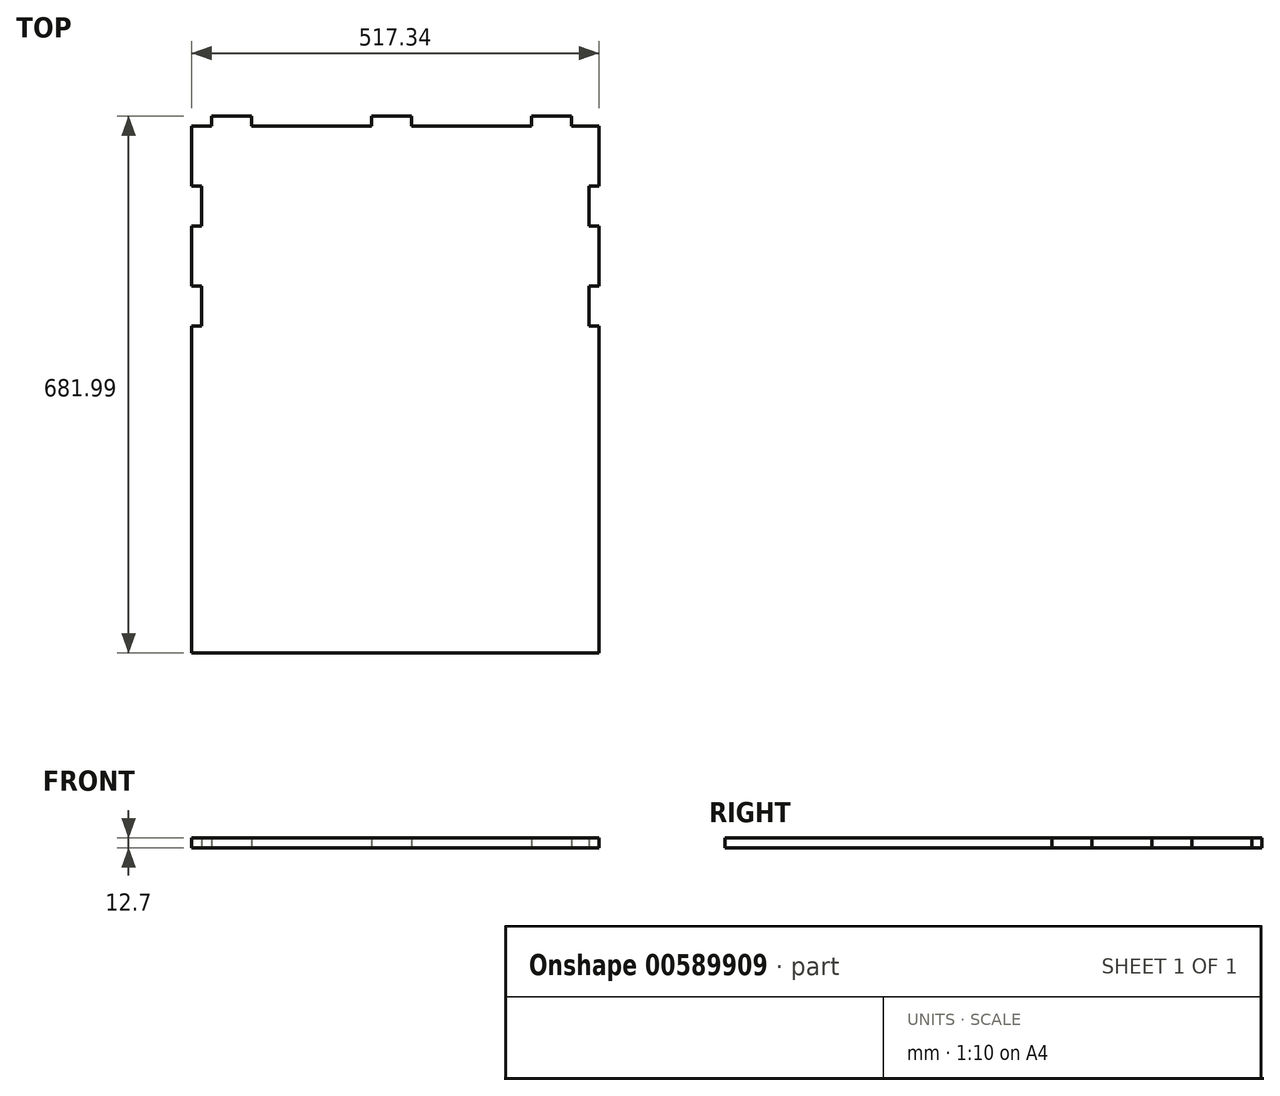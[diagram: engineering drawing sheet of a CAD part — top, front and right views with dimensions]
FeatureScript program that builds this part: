
annotation { "Feature Type Name" : "Feature", "Feature Type Description" : "" }
export const myFeature = defineFeature(function(context is Context, id is Id, definition is map)
    precondition{}
    {
        {
            var Q0;
            Q0=qCreatedBy(makeId("Top.planeOp"),FACE);
            var sketch = newSketch(context, id + "F0", { "sketchPlane" : qUnion([Q0])});
            skLineSegment(sketch, "E0.bottom", {"start": v(-296.76, 491.23) * mm, "end": v(-271.36, 491.23) * mm});
            skLineSegment(sketch, "E0.top", {"start": v(-296.76, -178.06) * mm, "end": v(220.58, -178.06) * mm});
            skLineSegment(sketch, "E0.left", {"start": v(-296.76, 491.23) * mm, "end": v(-296.76, 415.03) * mm});
            skLineSegment(sketch, "E0.right", {"start": v(220.58, 491.23) * mm, "end": v(220.58, 415.03) * mm});
            skLineSegment(sketch, "E1.top", {"start": v(-271.36, 503.93) * mm, "end": v(-220.56, 503.93) * mm});
            skLineSegment(sketch, "E1.left", {"start": v(-271.36, 491.23) * mm, "end": v(-271.36, 503.93) * mm});
            skLineSegment(sketch, "E1.right", {"start": v(-220.56, 491.23) * mm, "end": v(-220.56, 503.93) * mm});
            skLineSegment(sketch, "E2.top", {"start": v(185.84, 503.93) * mm, "end": v(135.04, 503.93) * mm});
            skLineSegment(sketch, "E2.left", {"start": v(185.84, 491.23) * mm, "end": v(185.84, 503.93) * mm});
            skLineSegment(sketch, "E2.right", {"start": v(135.04, 491.23) * mm, "end": v(135.04, 503.93) * mm});
            skLineSegment(sketch, "E3.top", {"start": v(-68.16, 503.93) * mm, "end": v(-17.36, 503.93) * mm});
            skLineSegment(sketch, "E3.left", {"start": v(-68.16, 491.23) * mm, "end": v(-68.16, 503.93) * mm});
            skLineSegment(sketch, "E3.right", {"start": v(-17.36, 491.23) * mm, "end": v(-17.36, 503.93) * mm});
            skLineSegment(sketch, "E4.bottom", {"start": v(220.58, 237.23) * mm, "end": v(207.88, 237.23) * mm});
            skLineSegment(sketch, "E4.top", {"start": v(220.58, 288.03) * mm, "end": v(207.88, 288.03) * mm});
            skLineSegment(sketch, "E4.right", {"start": v(207.88, 237.23) * mm, "end": v(207.88, 288.03) * mm});
            skLineSegment(sketch, "E5.bottom", {"start": v(-296.76, 415.03) * mm, "end": v(-284.06, 415.03) * mm});
            skLineSegment(sketch, "E5.top", {"start": v(-296.76, 364.23) * mm, "end": v(-284.06, 364.23) * mm});
            skLineSegment(sketch, "E5.right", {"start": v(-284.06, 415.03) * mm, "end": v(-284.06, 364.23) * mm});
            skLineSegment(sketch, "E6.bottom", {"start": v(-296.76, 288.03) * mm, "end": v(-284.06, 288.03) * mm});
            skLineSegment(sketch, "E6.top", {"start": v(-296.76, 237.23) * mm, "end": v(-284.06, 237.23) * mm});
            skLineSegment(sketch, "E6.right", {"start": v(-284.06, 288.03) * mm, "end": v(-284.06, 237.23) * mm});
            skLineSegment(sketch, "E7.bottom", {"start": v(220.58, 364.23) * mm, "end": v(207.88, 364.23) * mm});
            skLineSegment(sketch, "E7.top", {"start": v(220.58, 415.03) * mm, "end": v(207.88, 415.03) * mm});
            skLineSegment(sketch, "E7.right", {"start": v(207.88, 364.23) * mm, "end": v(207.88, 415.03) * mm});
            skLineSegment(sketch, "E8.trimOffspring", {"start": v(-296.76, 364.23) * mm, "end": v(-296.76, 288.03) * mm});
            skLineSegment(sketch, "E9.trimOffspring", {"start": v(-296.76, 237.23) * mm, "end": v(-296.76, -178.06) * mm});
            skLineSegment(sketch, "E10.trimOffspring", {"start": v(-220.56, 491.23) * mm, "end": v(-68.16, 491.23) * mm});
            skLineSegment(sketch, "E11.trimOffspring", {"start": v(-17.36, 491.23) * mm, "end": v(135.04, 491.23) * mm});
            skLineSegment(sketch, "E12.trimOffspring", {"start": v(185.84, 491.23) * mm, "end": v(220.58, 491.23) * mm});
            skLineSegment(sketch, "E13.trimOffspring", {"start": v(220.58, 364.23) * mm, "end": v(220.58, 288.03) * mm});
            skLineSegment(sketch, "E14.trimOffspring", {"start": v(220.58, 237.23) * mm, "end": v(220.58, -178.06) * mm});
            skSolve(sketch);
        }
        {
            var Q0;
            Q0 = qSketchRegion(id + "F0", true);
            extrude(context, id + "F1", {"entities" : qUnion([Q0]), "depth" : 12.7 * mm, "offsetDistance" : 25.4 * mm});
        }
    });
